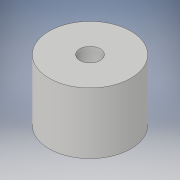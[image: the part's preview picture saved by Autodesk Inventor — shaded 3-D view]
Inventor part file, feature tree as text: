
AUTODESK INVENTOR PART (.ipt)
format: ipt  version: 2019 (Build 230136000, 136)  size: 92,672 bytes
history: native  units: mm
features: extrude x1, sketch x1
ambient origin geometry x8: Origin, YZ Plane, XZ Plane, XY Plane, X Axis, Y Axis, Z Axis, Center Point
bodies: Solid1 (feature_tree)
feature tree (2):
  extrude  "Extrusion1"  Depth=15.0mm
  sketch  "Sketch1"  dims[d0=20.0mm d1=5.0mm d2=15.0mm d3=0.0mm]
